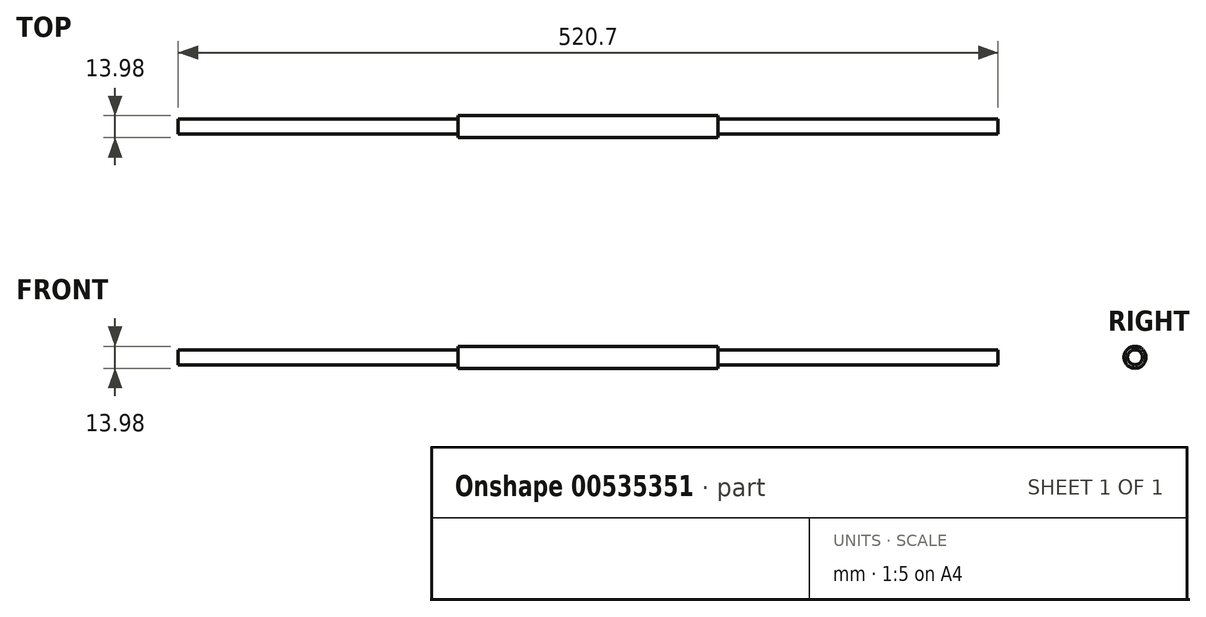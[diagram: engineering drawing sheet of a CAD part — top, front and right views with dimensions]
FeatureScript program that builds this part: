
annotation { "Feature Type Name" : "Feature", "Feature Type Description" : "" }
export const myFeature = defineFeature(function(context is Context, id is Id, definition is map)
    precondition{}
    {
        {
            var Q0;
            Q0=qCreatedBy(makeId("Front.planeOp"),FACE);
            var sketch = newSketch(context, id + "F0", { "sketchPlane" : qUnion([Q0])});
            skLineSegment(sketch, "E0", {"start": v(0, 0) * mm, "end": v(-520.7, 0) * mm});
            skLineSegment(sketch, "E1", {"start": v(-520.7, 0) * mm, "end": v(-520.7, 4.76) * mm});
            skLineSegment(sketch, "E2", {"start": v(-520.7, 4.76) * mm, "end": v(-342.9, 4.76) * mm});
            skLineSegment(sketch, "E3", {"start": v(-342.9, 4.76) * mm, "end": v(-342.9, 6.98) * mm});
            skLineSegment(sketch, "E4", {"start": v(-342.9, 6.98) * mm, "end": v(-177.8, 6.98) * mm});
            skLineSegment(sketch, "E5", {"start": v(-177.8, 6.98) * mm, "end": v(-177.8, 4.76) * mm});
            skLineSegment(sketch, "E6", {"start": v(-177.8, 4.76) * mm, "end": v(0, 4.76) * mm});
            skLineSegment(sketch, "E7", {"start": v(0, 4.76) * mm, "end": v(0, 0) * mm});
            skLineSegment(sketch, "E8", {"start": v(-177.8, 4.76) * mm, "end": v(-342.9, 4.76) * mm, "construction": true});
            skLineSegment(sketch, "E9", {"start": v(0, 0) * mm, "end": v(276.65, 0) * mm, "construction": true});
            skSolve(sketch);
        }
        {
            var Q0;
            Q0=makeQuery(id+"F0.imprint","IMPRINT",FACE,{"disambiguationData":[TD([[makeQuery(id+"F0.imprint","IMPRINT",EDGE,{"derivedFrom":sQuery(id+"F0.wireOp",EDGE,"E0")}),-1.0]])]});
            var Q1;
            Q1=sQuery(id+"F0.wireOp",EDGE,"E9");
            revolve(context, id + "F1", {"entities" : qUnion([Q0]), "axis" : qUnion([Q1]), "revolveType" : RevolveType.FULL});
        }
    });
